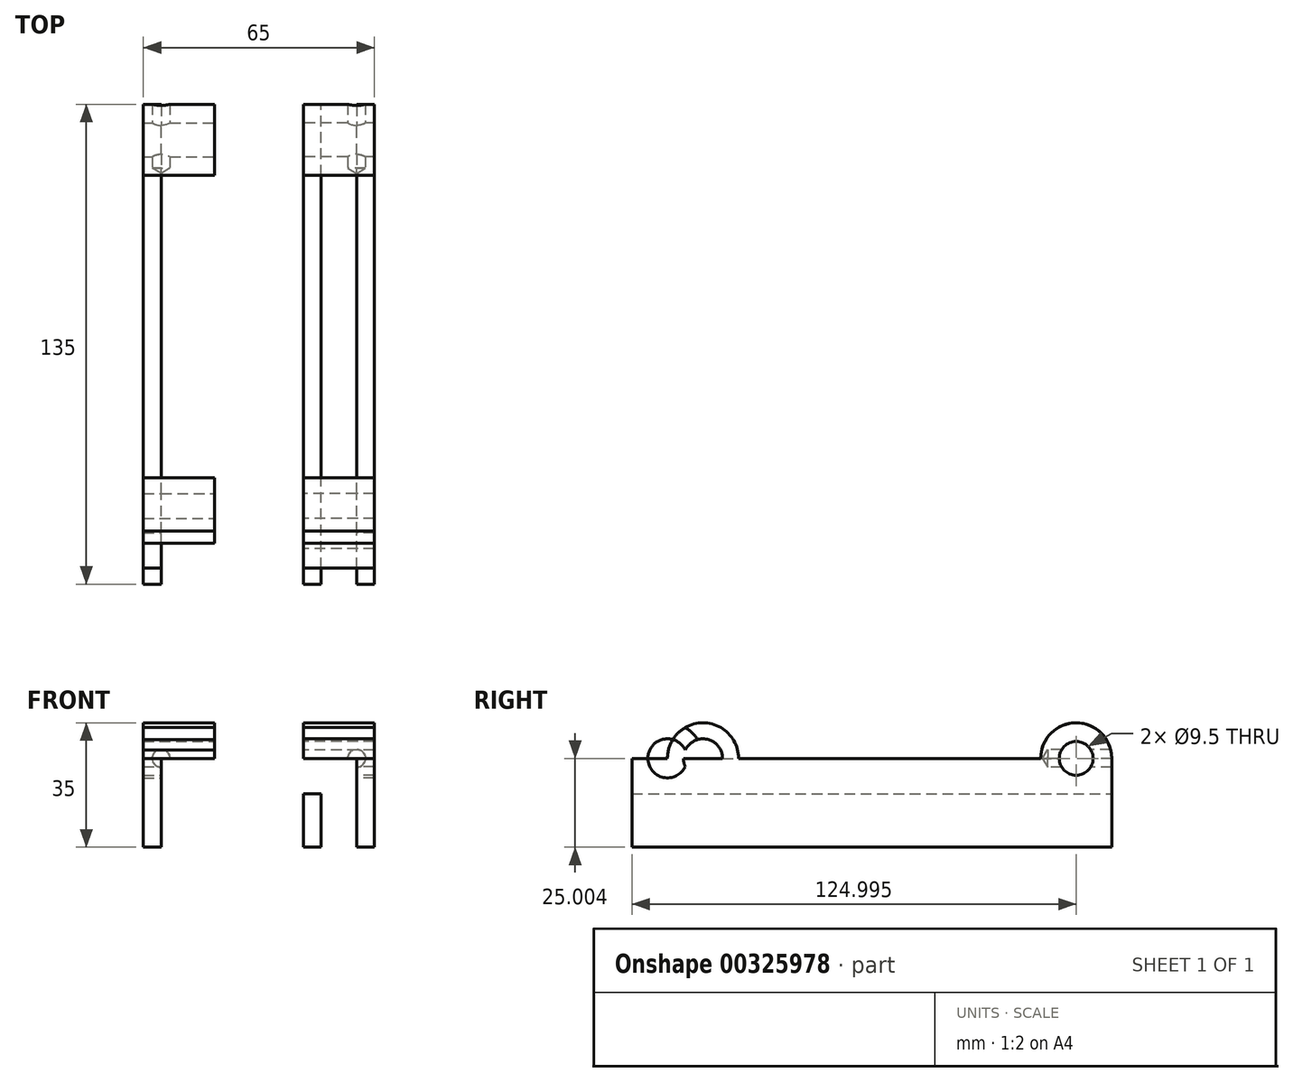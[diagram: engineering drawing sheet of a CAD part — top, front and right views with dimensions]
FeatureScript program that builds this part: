
annotation { "Feature Type Name" : "Feature", "Feature Type Description" : "" }
export const myFeature = defineFeature(function(context is Context, id is Id, definition is map)
    precondition{}
    {
        {
            var Q0;
            Q0=qCreatedBy(makeId("Right.planeOp"),FACE);
            var sketch = newSketch(context, id + "F0", { "sketchPlane" : qUnion([Q0])});
            skLineSegment(sketch, "E0.bottom", {"start": v(-59.32, 6.76) * mm, "end": v(75.68, 6.76) * mm});
            skLineSegment(sketch, "E0.top", {"start": v(-59.32, -3.24) * mm, "end": v(75.68, -3.24) * mm});
            skLineSegment(sketch, "E0.left", {"start": v(-59.32, 6.76) * mm, "end": v(-59.32, -3.24) * mm});
            skLineSegment(sketch, "E0.right", {"start": v(75.68, 6.76) * mm, "end": v(75.68, -3.24) * mm});
            skLineSegment(sketch, "E1.top", {"start": v(-59.32, -18.24) * mm, "end": v(75.68, -18.24) * mm});
            skLineSegment(sketch, "E1.left", {"start": v(-59.32, -3.24) * mm, "end": v(-59.32, -18.24) * mm});
            skLineSegment(sketch, "E1.right", {"start": v(75.68, -3.24) * mm, "end": v(75.68, -18.24) * mm});
            skArc(sketch, "E2", {"start": v(75.68, 6.76) * mm, "mid": v(65.68, 16.76) * mm, "end": v(55.68, 6.76) * mm});
            skArc(sketch, "E3", {"start": v(-39.32, 6.76) * mm, "mid": v(-49.32, 16.76) * mm, "end": v(-59.32, 6.76) * mm});
            skArc(sketch, "E4", {"start": v(-49.32, 6.76) * mm, "mid": v(-39.32, 16.76) * mm, "end": v(-29.32, 6.76) * mm});
            skCircle(sketch, "E5", {"center": v(-49.32, 6.76) * mm, "radius": 5.5 * mm});
            skCircle(sketch, "E6", {"center": v(-39.32, 6.76) * mm, "radius": 5.5 * mm});
            skCircle(sketch, "E7", {"center": v(65.68, 6.76) * mm, "radius": 4.75 * mm});
            skSolve(sketch);
        }
        {
            var Q0;
            {var subQ0=sQuery(id+"F0.wireOp",EDGE,"E3");var subQ5=sQuery(id+"F0.wireOp",EDGE,"E4");var subQ6=makeQuery(id+"F0.imprint","INTERSECT",VERTEX,{"derivedFrom":[subQ0,subQ5]});Q0=makeQuery(id+"F0.imprint","IMPRINT",FACE,{"disambiguationData":[TD([[makeQuery(id+"F0.imprint","IMPRINT",EDGE,{"disambiguationData":[TD([[subQ6,1.0]])],"derivedFrom":subQ5}),1.0]])]});}
            var Q1;
            {var subQ0=sQuery(id+"F0.wireOp",EDGE,"E4");var subQ1=sQuery(id+"F0.wireOp",EDGE,"E0.bottom");var subQ2=makeQuery(id+"F0.imprint","INTERSECT",VERTEX,{"disambiguationData":[OD(1.0)],"derivedFrom":[subQ1,subQ0]});Q1=makeQuery(id+"F0.imprint","IMPRINT",FACE,{"disambiguationData":[TD([[makeQuery(id+"F0.imprint","IMPRINT",EDGE,{"disambiguationData":[TD([[subQ2,1.0]])],"derivedFrom":subQ1}),1.0]])]});}
            var Q2;
            {var subQ0=sQuery(id+"F0.wireOp",EDGE,"E4");var subQ1=sQuery(id+"F0.wireOp",EDGE,"E3");var subQ2=makeQuery(id+"F0.imprint","INTERSECT",VERTEX,{"derivedFrom":[subQ1,subQ0]});Q2=makeQuery(id+"F0.imprint","IMPRINT",FACE,{"disambiguationData":[TD([[makeQuery(id+"F0.imprint","IMPRINT",EDGE,{"disambiguationData":[TD([[subQ2,1.0]])],"derivedFrom":subQ1}),1.0]])]});}
            var Q3;
            {var subQ11=sQuery(id+"F0.wireOp",EDGE,"E0.left");Q3=makeQuery(id+"F0.imprint","IMPRINT",FACE,{"disambiguationData":[TD([[makeQuery(id+"F0.imprint","IMPRINT",EDGE,{"derivedFrom":subQ11}),1.0]])]});}
            var Q4;
            {var subQ0=sQuery(id+"F0.wireOp",EDGE,"E2");Q4=makeQuery(id+"F0.imprint","IMPRINT",FACE,{"disambiguationData":[TD([[makeQuery(id+"F0.imprint","IMPRINT",EDGE,{"derivedFrom":subQ0}),1.0]])]});}
            extrude(context, id + "F1", {"entities" : qUnion([Q0, Q1, Q2, Q3, Q4]), "depth" : 20 * mm, "offsetDistance" : 25 * mm});
        }
        {
            var Q0;
            Q0=makeQuery(id+"F0.imprint","IMPRINT",FACE,{"disambiguationData":[TD([[makeQuery(id+"F0.imprint","IMPRINT",EDGE,{"derivedFrom":sQuery(id+"F0.wireOp",EDGE,"E0.top")}),-1.0]])]});
            extrude(context, id + "F2", {"entities" : qUnion([Q0]), "operationType" : NewBodyOperationType.ADD, "depth" : 5 * mm, "offsetDistance" : 25 * mm});
        }
        {
            var Q0;
            Q0=makeQuery(id+"F2.opExtrude","CAP_FACE",FACE,{"disambiguationData":[OSD([sQuery(id+"F0.wireOp",EDGE,"E0.top"),sQuery(id+"F0.wireOp",EDGE,"E1.top"),sQuery(id+"F0.wireOp",EDGE,"E1.left"),sQuery(id+"F0.wireOp",EDGE,"E1.right")])],"isStart":false});
            extrude(context, id + "F3", {"entities" : qUnion([Q0]), "operationType" : NewBodyOperationType.ADD, "depth" : 15 * mm, "offsetDistance" : 25 * mm, "hasSecondDirection" : true, "secondDirectionOppositeDirection" : false, "secondDirectionDepth" : 10 * mm});
        }
        {
            var Q0;
            {var subQ0=sQuery(id+"F0.wireOp",EDGE,"E0.bottom");var subQ1=makeQuery(id+"F0.imprint","INTERSECT",VERTEX,{"disambiguationData":[OD(0.0)],"derivedFrom":[subQ0,sQuery(id+"F0.wireOp",EDGE,"E4")]});Q0=makeQuery(id+"F0.imprint","IMPRINT",FACE,{"disambiguationData":[TD([[makeQuery(id+"F0.imprint","IMPRINT",EDGE,{"disambiguationData":[TD([[subQ1,1.0]])],"derivedFrom":subQ0}),-1.0]])]});}
            var Q1;
            {var subQ0=sQuery(id+"F0.wireOp",EDGE,"E0.bottom");var subQ1=makeQuery(id+"F0.imprint","INTERSECT",VERTEX,{"derivedFrom":[subQ0,sQuery(id+"F0.wireOp",EDGE,"E3")]});Q1=makeQuery(id+"F0.imprint","IMPRINT",FACE,{"disambiguationData":[TD([[makeQuery(id+"F0.imprint","IMPRINT",EDGE,{"disambiguationData":[TD([[subQ1,1.0]])],"derivedFrom":subQ0}),-1.0]])]});}
            var Q2;
            {var subQ0=sQuery(id+"F0.wireOp",EDGE,"E6");var subQ1=sQuery(id+"F0.wireOp",EDGE,"E0.bottom");var subQ2=makeQuery(id+"F0.imprint","INTERSECT",VERTEX,{"disambiguationData":[OD(0.0)],"derivedFrom":[subQ1,subQ0]});Q2=makeQuery(id+"F0.imprint","IMPRINT",FACE,{"disambiguationData":[TD([[makeQuery(id+"F0.imprint","IMPRINT",EDGE,{"disambiguationData":[TD([[subQ2,-1.0]])],"derivedFrom":subQ1}),-1.0]])]});}
            extrude(context, id + "F4", {"entities" : qUnion([Q0, Q1, Q2]), "operationType" : NewBodyOperationType.ADD, "depth" : 20 * mm, "offsetDistance" : 25 * mm, "hasSecondDirection" : true, "secondDirectionOppositeDirection" : false, "secondDirectionDepth" : 15 * mm});
        }
        {
            var Q0;
            {var subQ0=sQuery(id+"F0.wireOp",EDGE,"E1.right");Q0=makeQuery(id+"F3.boolean.opBoolean","MERGE",FACE,{"derivedFrom":[makeQuery(id+"F2.boolean.opBoolean","MERGE",FACE,{"derivedFrom":[makeQuery(id+"F1.opExtrude","SWEPT_FACE",FACE,{"disambiguationData":[OSD([sQuery(id+"F0.wireOp",EDGE,"E0.right")])]}),makeQuery(id+"F2.opExtrude","SWEPT_FACE",FACE,{"disambiguationData":[OSD([subQ0])]})]}),makeQuery(id+"F3.opExtrude","SWEPT_FACE",FACE,{"disambiguationData":[OSD([subQ0])]})]});}
            var sketch = newSketch(context, id + "F5", { "sketchPlane" : qUnion([Q0])});
            skLineSegment(sketch, "E8.0.0", {"start": v(0, -18.24) * mm, "end": v(0, 6.76) * mm});
            skLineSegment(sketch, "E8.0.1", {"start": v(0, 6.76) * mm, "end": v(-20, 6.76) * mm});
            skLineSegment(sketch, "E8.0.2", {"start": v(-20, 6.76) * mm, "end": v(-20, -18.24) * mm});
            skLineSegment(sketch, "E8.0.3", {"start": v(-20, -18.24) * mm, "end": v(-15, -18.24) * mm});
            skLineSegment(sketch, "E8.0.4", {"start": v(-15, -18.24) * mm, "end": v(-15, -3.24) * mm});
            skLineSegment(sketch, "E8.0.5", {"start": v(-15, -3.24) * mm, "end": v(-5, -3.24) * mm});
            skLineSegment(sketch, "E8.0.6", {"start": v(-5, -3.24) * mm, "end": v(-5, -18.24) * mm});
            skLineSegment(sketch, "E8.0.7", {"start": v(-5, -18.24) * mm, "end": v(0, -18.24) * mm});
            skLineSegment(sketch, "E9", {"start": v(-20, 16.76) * mm, "end": v(0, 16.76) * mm});
            skPoint(sketch, "E10", {"position": v(-15, 6.76) * mm});
            skSolve(sketch);
        }
        {
            var Q0;
            Q0=sQuery(id+"F5.wireOp",VERTEX,"E10");
            var Q1;
            Q1=makeQuery(id+"F1.opExtrude","SWEPT_BODY",BODY,{"disambiguationData":[OSD([sQuery(id+"F0.wireOp",EDGE,"E0.bottom"),sQuery(id+"F0.wireOp",EDGE,"E0.left"),sQuery(id+"F0.wireOp",EDGE,"E0.right"),sQuery(id+"F0.wireOp",EDGE,"E0.top"),sQuery(id+"F0.wireOp",EDGE,"E2"),sQuery(id+"F0.wireOp",EDGE,"E3"),sQuery(id+"F0.wireOp",EDGE,"E4"),sQuery(id+"F0.wireOp",EDGE,"E5"),sQuery(id+"F0.wireOp",EDGE,"E6"),sQuery(id+"F0.wireOp",EDGE,"E7")])]});
            hole(context, id + "F6", {"style" : HoleStyle.SIMPLE, "endStyle" : HoleEndStyle.BLIND, "holeDiameter" : 5 * mm, "majorDiameter" : 5 * mm, "holeDepth" : 12 * mm, "tappedDepth" : 12 * mm, "tapClearance" : 3, "locations" : qUnion([Q0]), "scope" : qUnion([Q1]), "startStyle" : HoleStartStyle.PART});
        }
        {
            var Q0;
            Q0=makeQuery(id+"F1.opExtrude","SWEPT_BODY",BODY,{"disambiguationData":[OSD([sQuery(id+"F0.wireOp",EDGE,"E0.bottom"),sQuery(id+"F0.wireOp",EDGE,"E0.left"),sQuery(id+"F0.wireOp",EDGE,"E0.right"),sQuery(id+"F0.wireOp",EDGE,"E0.top"),sQuery(id+"F0.wireOp",EDGE,"E2"),sQuery(id+"F0.wireOp",EDGE,"E3"),sQuery(id+"F0.wireOp",EDGE,"E4"),sQuery(id+"F0.wireOp",EDGE,"E5"),sQuery(id+"F0.wireOp",EDGE,"E6"),sQuery(id+"F0.wireOp",EDGE,"E7")])]});
            var Q1;
            Q1=qCreatedBy(makeId("Right.planeOp"),FACE);
            mirror(context, id + "F7", {"entities" : qUnion([Q0]), "mirrorPlane" : qUnion([Q1])});
        }
        {
            var Q0;
            Q0=makeQuery(id+"F7.opPattern","COPY",BODY,{"derivedFrom":makeQuery(id+"F1.opExtrude","SWEPT_BODY",BODY,{"disambiguationData":[OSD([sQuery(id+"F0.wireOp",EDGE,"E0.bottom"),sQuery(id+"F0.wireOp",EDGE,"E0.left"),sQuery(id+"F0.wireOp",EDGE,"E0.right"),sQuery(id+"F0.wireOp",EDGE,"E0.top"),sQuery(id+"F0.wireOp",EDGE,"E2"),sQuery(id+"F0.wireOp",EDGE,"E3"),sQuery(id+"F0.wireOp",EDGE,"E4"),sQuery(id+"F0.wireOp",EDGE,"E5"),sQuery(id+"F0.wireOp",EDGE,"E6"),sQuery(id+"F0.wireOp",EDGE,"E7")])]}),"instanceName":"1"});
            var Q1;
            Q1=qCreatedBy(makeId("Right.planeOp"),FACE);
            transform(context, id + "F8", {"entities" : qUnion([Q0]), "transformType" : TransformType.TRANSLATION_DISTANCE, "transformDirection" : qUnion([Q1]), "distance" : 25 * mm, "oppositeDirection" : true, "makeCopy" : false});
        }
    });
